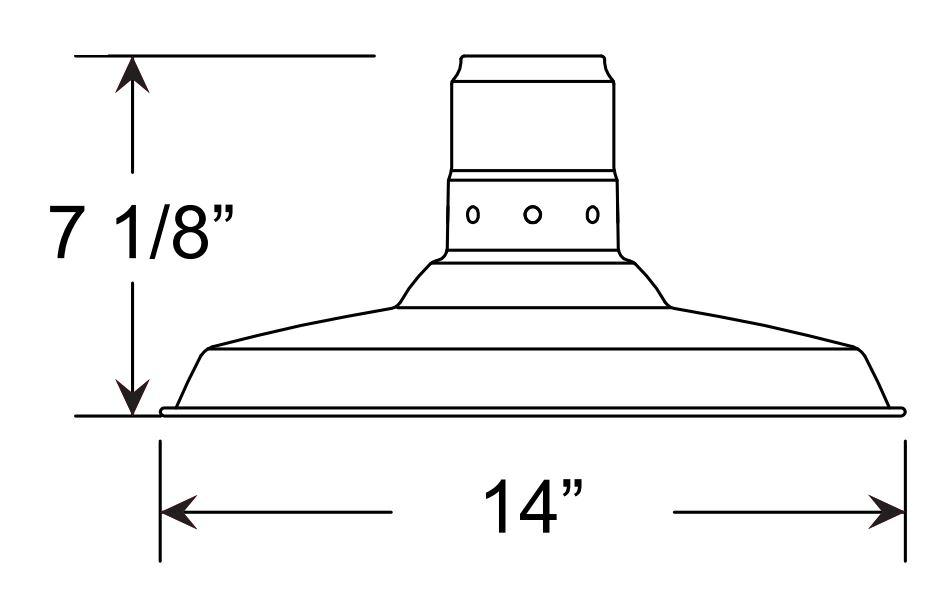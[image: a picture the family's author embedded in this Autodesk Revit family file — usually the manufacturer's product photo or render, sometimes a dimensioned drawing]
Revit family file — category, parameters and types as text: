
# Revit family: OSGGF Metal Fabric MB 24,30,36
name_source: partatom
category: Lighting Fixtures
units: mm (PartAtom-declared; Revit-internal decimal feet)

## family parameters
Always vertical = Yes
Cut with Voids When Loaded = No
Light Source = Yes
OmniClass Number = 23.80.70.00
OmniClass Title = Lighting
Part Type = Normal
Room Calculation Point = No
Round Connector Dimension = Use Diameter
Shared = No
Work Plane-Based = No

## types (3) — shared parameters
Apparent Load = 200 VA
Body Colour = Spun aluminium
Body Material = body
Bulb = Glass
CRI = >90
Canopy Body = GY
Color Filter = 16777215
Construction Material = Heavy Duty spun aluminum.
Default Elevation = 0' - 0"
Description = 120-277 Voltage
Dimming = 1%
Dimming Lamp Color Temperature Shift = <None>
Efficiency = 97-125 lumens per watt
HUB = Texture Black
Lamp = MB
Life = L70 50,000 hours
Load Classification = Lighting
Manufacturer = ANP Lighting
Photometric Web File = generic
Power Factor = 1
Tilt Angle = 90.00°
URL = https://www.anplighting.com
Voltage = 120 V
Warranty = 5 year limited warranty
b = 0' - 3"

## per-type parameters (varying)
| type | Fixture Diameter | Fixture Height | OSGGF24 | OSGGF30 | OSGGF36 | Wattage Comments | Weight | a |
| OSGGF24 | 2' - 0" | 2' - 2 1/2" | Yes | No | No | 200 W | 11.0 lbs | 1' - 10" |
| OSGGF30 | 2' - 6" | 2' - 9" | No | Yes | No | 200W | 16.5 lbs | 2' - 7" |
| OSGGF36 | 3' - 0" | 3' - 3 3/4" | No | No | Yes | 200W | 22.0 lbs | 2' - 9" |

note: column(s) folded — value = type name in every type: Model

## geometry (parser evidence)
native form markers: Sweep x28
no freeform markers — native parametric forms only
